# Revit family: Lin2-9.84ft-Double Head
name_source: partatom
category: Lighting Fixtures
units: mm (PartAtom-declared; Revit-internal decimal feet)

## family parameters
Always vertical = Yes
Cut with Voids When Loaded = No
Light Source = No
Maintain Annotation Orientation = No
OmniClass Number = 23.80.70.00
OmniClass Title = Lighting
Part Type = Normal
Room Calculation Point = No
Round Connector Dimension = Use Diameter
Shared = No
Work Plane-Based = No

## types (16) — shared parameters
CRI = 80
Default Elevation = 0' - 0"
H = 9' - 10 3/32"
IP Rating = IP65
Input Voltage = 120-277V
Lamp = LED
Load Classification = Lighting
Manufacturer = Above All Lighting
Power Factor = 0.9
URL = https://www.abovealllighting.com

## per-type parameters (varying)
| type | IES | Model | Wattage Comments |
| LIN2-70W-3000K-II-9.84ft | LIN2 IES : 70W-II | LIN2-7030801-II-BK | 70W |
| LIN2-70W-3000K-III-9.84ft | LIN2 IES : 70W-III | LIN2-7030801-III-BK | 70W |
| LIN2-70W-3000K-IV-9.84ft | LIN2 IES : 70W-IV | LIN2-7030801-IV-BK | 70W |
| LIN2-70W-3000K-V-9.84ft | LIN2 IES : 70W-V | LIN2-7030801-V-BK | 70W |
| LIN2-80W-3000K-II-9.84ft | LIN2 IES : 80W-II | LIN2-8030801-II-BK | 80W |
| LIN2-80W-3000K-III-9.84ft | LIN2 IES : 80W-III | LIN2-8030801-III-BK | 80W |
| LIN2-80W-3000K-IV-9.84ft | LIN2 IES : 80W-IV | LIN2-8030801-IV-BK | 80W |
| LIN2-80W-3000K-V-9.84ft | LIN2 IES : 80W-V | LIN2-8030801-V-BK | 80W |
| LIN2-100W-3000K-II-9.84ft | LIN2 IES : 100W-II | LIN2-10030801-II-BK | 100W |
| LIN2-100W-3000K-III-9.84ft | LIN2 IES : 100W-III | LIN2-10030801-III-BK | 100W |
| LIN2-100W-3000K-IV-9.84ft | LIN2 IES : 100W-IV | LIN2-10030801-IV-BK | 100W |
| LIN2-100W-3000K-V-9.84ft | LIN2 IES : 100W-V | LIN2-10030801-V-BK | 100W |
| LIN2-120W-3000K-II-9.84ft | LIN2 IES : 120W-II | LIN2-12030801-II-BK | 120W |
| LIN2-120W-3000K-III-9.84ft | LIN2 IES : 120W-III | LIN2-12030801-III-BK | 120W |
| LIN2-120W-3000K-IV-9.84ft | LIN2 IES : 120W-IV | LIN2-12030801-IV-BK | 120W |
| LIN2-120W-3000K-V-9.84ft | LIN2 IES : 120W-V | LIN2-12030801-V-BK | 120W |

## geometry (parser evidence)
native form markers: Sweep x5
no freeform markers — native parametric forms only
